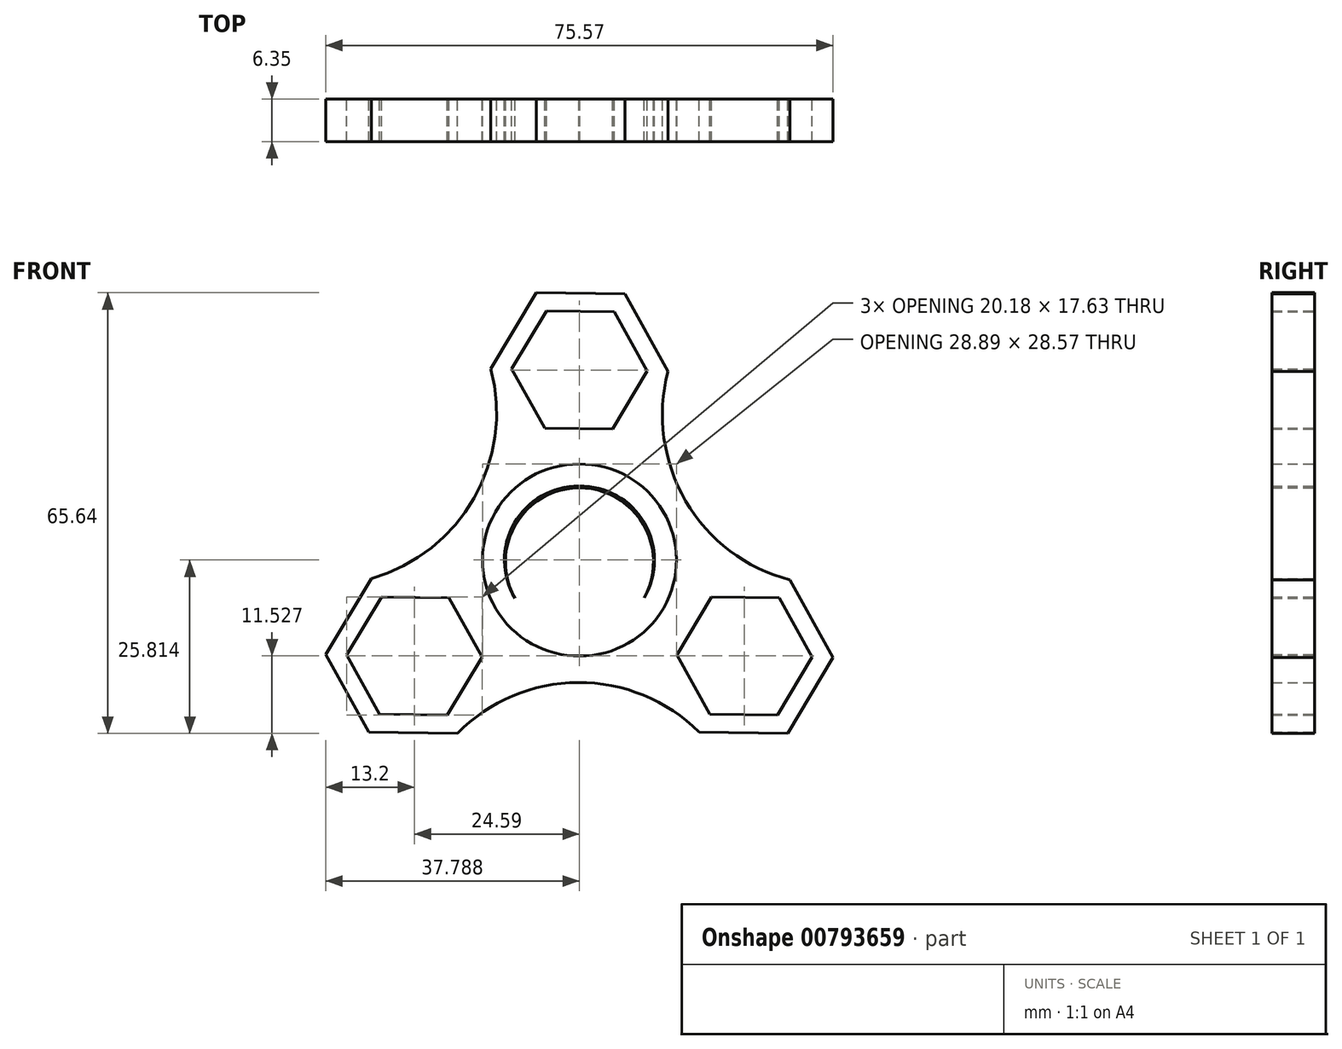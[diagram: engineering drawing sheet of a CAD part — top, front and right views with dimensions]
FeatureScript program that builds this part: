
annotation { "Feature Type Name" : "Feature", "Feature Type Description" : "" }
export const myFeature = defineFeature(function(context is Context, id is Id, definition is map)
    precondition{}
    {
        {
            var Q0;
            Q0=qCreatedBy(makeId("Front.planeOp"),FACE);
            var sketch = newSketch(context, id + "F0", { "sketchPlane" : qUnion([Q0])});
            skCircle(sketch, "E0", {"center": v(0, 0) * mm, "radius": 14.29 * mm});
            skCircle(sketch, "E1", {"center": v(0, 0) * mm, "radius": 11.02 * mm});
            skCircle(sketch, "E2.cCircle", {"center": v(0, 28.58) * mm, "radius": 11.43 * mm, "construction": true});
            skLineSegment(sketch, "E2.0", {"start": v(13.2, 28.38) * mm, "end": v(6.43, 17.05) * mm});
            skLineSegment(sketch, "E2.1", {"start": v(6.43, 17.05) * mm, "end": v(-6.77, 17.24) * mm});
            skLineSegment(sketch, "E2.2", {"start": v(-6.77, 17.24) * mm, "end": v(-13.2, 28.77) * mm});
            skLineSegment(sketch, "E2.3", {"start": v(-13.2, 28.77) * mm, "end": v(-6.43, 40.1) * mm});
            skLineSegment(sketch, "E2.4", {"start": v(-6.43, 40.1) * mm, "end": v(6.77, 39.9) * mm});
            skLineSegment(sketch, "E2.5", {"start": v(6.77, 39.9) * mm, "end": v(13.2, 28.38) * mm});
            skPoint(sketch, "E2.0.midPoint", {"position": v(9.81, 22.71) * mm});
            skCircle(sketch, "E3.cCircle", {"center": v(0, 28.58) * mm, "radius": 8.74 * mm, "construction": true});
            skLineSegment(sketch, "E3.0", {"start": v(10.09, 28.42) * mm, "end": v(4.91, 19.76) * mm});
            skLineSegment(sketch, "E3.1", {"start": v(4.91, 19.76) * mm, "end": v(-5.18, 19.91) * mm});
            skLineSegment(sketch, "E3.2", {"start": v(-5.18, 19.91) * mm, "end": v(-10.09, 28.73) * mm});
            skLineSegment(sketch, "E3.3", {"start": v(-10.09, 28.73) * mm, "end": v(-4.91, 37.39) * mm});
            skLineSegment(sketch, "E3.4", {"start": v(-4.91, 37.39) * mm, "end": v(5.18, 37.24) * mm});
            skLineSegment(sketch, "E3.5", {"start": v(5.18, 37.24) * mm, "end": v(10.09, 28.42) * mm});
            skPoint(sketch, "E3.0.midPoint", {"position": v(7.5, 24.1) * mm});
            skPoint(sketch, "E4.center", {"position": v(0, 7.31) * mm});
            skPoint(sketch, "E5.center", {"position": v(0, 10.49) * mm});
            skLineSegment(sketch, "E6.1.0", {"start": v(-31.36, -25.34) * mm, "end": v(-37.79, -13.82) * mm});
            skLineSegment(sketch, "E6.1.1", {"start": v(-11.4, -14.2) * mm, "end": v(-18.16, -25.54) * mm});
            skLineSegment(sketch, "E6.1.2", {"start": v(-31.02, -2.49) * mm, "end": v(-17.82, -2.68) * mm});
            skLineSegment(sketch, "E6.1.3", {"start": v(-18.16, -25.54) * mm, "end": v(-31.36, -25.34) * mm});
            skCircle(sketch, "E6.1.4", {"center": v(-24.59, -14.01) * mm, "radius": 8.74 * mm, "construction": true});
            skCircle(sketch, "E6.1.5", {"center": v(0.16, 0.27) * mm, "radius": 14.29 * mm});
            skPoint(sketch, "E6.1.6", {"position": v(-24.42, -2.58) * mm});
            skLineSegment(sketch, "E6.1.7", {"start": v(-14.5, -14.17) * mm, "end": v(-19.68, -22.83) * mm});
            skLineSegment(sketch, "E6.1.8", {"start": v(-17.82, -2.68) * mm, "end": v(-11.4, -14.2) * mm});
            skCircle(sketch, "E6.1.9", {"center": v(-24.59, -14.01) * mm, "radius": 11.43 * mm, "construction": true});
            skLineSegment(sketch, "E6.1.10", {"start": v(-19.41, -5.35) * mm, "end": v(-14.5, -14.17) * mm});
            skPoint(sketch, "E6.1.11", {"position": v(-24.46, -5.28) * mm});
            skCircle(sketch, "E6.1.12", {"center": v(0.16, 0.27) * mm, "radius": 11.02 * mm});
            skPoint(sketch, "E6.1.13", {"position": v(-8.93, -4.97) * mm});
            skLineSegment(sketch, "E6.1.14", {"start": v(-34.68, -13.86) * mm, "end": v(-29.5, -5.2) * mm});
            skLineSegment(sketch, "E6.1.15", {"start": v(-29.77, -22.67) * mm, "end": v(-34.68, -13.86) * mm});
            skLineSegment(sketch, "E6.1.16", {"start": v(-19.68, -22.83) * mm, "end": v(-29.77, -22.67) * mm});
            skLineSegment(sketch, "E6.1.17", {"start": v(-37.79, -13.82) * mm, "end": v(-31.02, -2.49) * mm});
            skPoint(sketch, "E6.1.18", {"position": v(-6.18, -3.38) * mm});
            skLineSegment(sketch, "E6.1.19", {"start": v(-29.5, -5.2) * mm, "end": v(-19.41, -5.35) * mm});
            skLineSegment(sketch, "E6.2.0", {"start": v(37.78, -14.21) * mm, "end": v(31.01, -25.54) * mm});
            skLineSegment(sketch, "E6.2.1", {"start": v(18.16, -2.49) * mm, "end": v(31.36, -2.68) * mm});
            skLineSegment(sketch, "E6.2.2", {"start": v(17.82, -25.34) * mm, "end": v(11.4, -13.82) * mm});
            skLineSegment(sketch, "E6.2.3", {"start": v(31.36, -2.68) * mm, "end": v(37.78, -14.21) * mm});
            skCircle(sketch, "E6.2.4", {"center": v(24.59, -14.01) * mm, "radius": 8.74 * mm, "construction": true});
            skCircle(sketch, "E6.2.5", {"center": v(-0.16, 0.27) * mm, "radius": 14.29 * mm});
            skPoint(sketch, "E6.2.6", {"position": v(14.6, -19.58) * mm});
            skLineSegment(sketch, "E6.2.7", {"start": v(19.68, -5.2) * mm, "end": v(29.76, -5.35) * mm});
            skLineSegment(sketch, "E6.2.8", {"start": v(11.4, -13.82) * mm, "end": v(18.16, -2.49) * mm});
            skCircle(sketch, "E6.2.9", {"center": v(24.59, -14.01) * mm, "radius": 11.43 * mm, "construction": true});
            skLineSegment(sketch, "E6.2.10", {"start": v(14.5, -13.86) * mm, "end": v(19.68, -5.2) * mm});
            skPoint(sketch, "E6.2.11", {"position": v(16.95, -18.27) * mm});
            skCircle(sketch, "E6.2.12", {"center": v(-0.16, 0.27) * mm, "radius": 11.02 * mm});
            skPoint(sketch, "E6.2.13", {"position": v(8.92, -4.97) * mm});
            skLineSegment(sketch, "E6.2.14", {"start": v(29.5, -22.83) * mm, "end": v(19.41, -22.67) * mm});
            skLineSegment(sketch, "E6.2.15", {"start": v(34.68, -14.17) * mm, "end": v(29.5, -22.83) * mm});
            skLineSegment(sketch, "E6.2.16", {"start": v(29.76, -5.35) * mm, "end": v(34.68, -14.17) * mm});
            skLineSegment(sketch, "E6.2.17", {"start": v(31.01, -25.54) * mm, "end": v(17.82, -25.34) * mm});
            skPoint(sketch, "E6.2.18", {"position": v(6.18, -3.38) * mm});
            skLineSegment(sketch, "E6.2.19", {"start": v(19.41, -22.67) * mm, "end": v(14.5, -13.86) * mm});
            skPoint(sketch, "E6.center", {"position": v(0, 0.18) * mm});
            skArc(sketch, "E7", {"start": v(-31.02, -2.49) * mm, "mid": v(-15.7, 9.5) * mm, "end": v(-13.2, 28.77) * mm});
            skArc(sketch, "E8", {"start": v(17.82, -25.34) * mm, "mid": v(-0.21, -17.97) * mm, "end": v(-18.16, -25.54) * mm});
            skArc(sketch, "E9", {"start": v(13.2, 28.38) * mm, "mid": v(15.83, 9.08) * mm, "end": v(31.36, -2.68) * mm});
            skSolve(sketch);
        }
        {
            var Q0;
            {var subQ1=sQuery(id+"F0.wireOp",EDGE,"E2.1");Q0=makeQuery(id+"F0.imprint","IMPRINT",FACE,{"disambiguationData":[TD([[makeQuery(id+"F0.imprint","IMPRINT",EDGE,{"derivedFrom":subQ1}),-1.0]])]});}
            var Q1;
            Q1=makeQuery(id+"F0.imprint","IMPRINT",FACE,{"disambiguationData":[TD([[makeQuery(id+"F0.imprint","IMPRINT",EDGE,{"derivedFrom":sQuery(id+"F0.wireOp",EDGE,"E1")}),-1.0]])]});
            var Q2;
            {var subQ1=sQuery(id+"F0.wireOp",EDGE,"E5.1.8");Q2=makeQuery(id+"F0.imprint","IMPRINT",FACE,{"disambiguationData":[TD([[makeQuery(id+"F0.imprint","IMPRINT",EDGE,{"derivedFrom":subQ1}),1.0]])]});}
            var Q3;
            Q3=makeQuery(id+"F0.imprint","IMPRINT",FACE,{"disambiguationData":[TD([[makeQuery(id+"F0.imprint","IMPRINT",EDGE,{"derivedFrom":sQuery(id+"F0.wireOp",EDGE,"E5.1.1")}),1.0]])]});
            var Q4;
            Q4=makeQuery(id+"F0.imprint","IMPRINT",FACE,{"disambiguationData":[TD([[makeQuery(id+"F0.imprint","IMPRINT",EDGE,{"derivedFrom":sQuery(id+"F0.wireOp",EDGE,"E5.2.1")}),1.0]])]});
            var Q5;
            {var subQ5=sQuery(id+"F0.wireOp",EDGE,"E6.1.5");var subQ6=sQuery(id+"F0.wireOp",EDGE,"E0");var subQ7=makeQuery(id+"F0.imprint","INTERSECT",VERTEX,{"disambiguationData":[OD(0.0)],"derivedFrom":[subQ6,subQ5]});Q5=makeQuery(id+"F0.imprint","IMPRINT",FACE,{"disambiguationData":[TD([[makeQuery(id+"F0.imprint","IMPRINT",EDGE,{"disambiguationData":[TD([[subQ7,1.0]])],"derivedFrom":subQ6}),1.0]])]});}
            var Q6;
            Q6=makeQuery(id+"F0.imprint","IMPRINT",FACE,{"disambiguationData":[TD([[makeQuery(id+"F0.imprint","IMPRINT",EDGE,{"derivedFrom":sQuery(id+"F0.wireOp",EDGE,"E6.2.0")}),-1.0]])]});
            var Q7;
            Q7=makeQuery(id+"F0.imprint","IMPRINT",FACE,{"disambiguationData":[TD([[makeQuery(id+"F0.imprint","IMPRINT",EDGE,{"derivedFrom":sQuery(id+"F0.wireOp",EDGE,"E2.0")}),1.0]])]});
            var Q8;
            Q8=makeQuery(id+"F0.imprint","IMPRINT",FACE,{"disambiguationData":[TD([[makeQuery(id+"F0.imprint","IMPRINT",EDGE,{"derivedFrom":sQuery(id+"F0.wireOp",EDGE,"E6.1.0")}),-1.0]])]});
            extrude(context, id + "F1", {"entities" : qUnion([Q0, Q1, Q2, Q3, Q4, Q5, Q6, Q7, Q8]), "depth" : 6.35 * mm, "offsetDistance" : 25.4 * mm});
        }
    });
